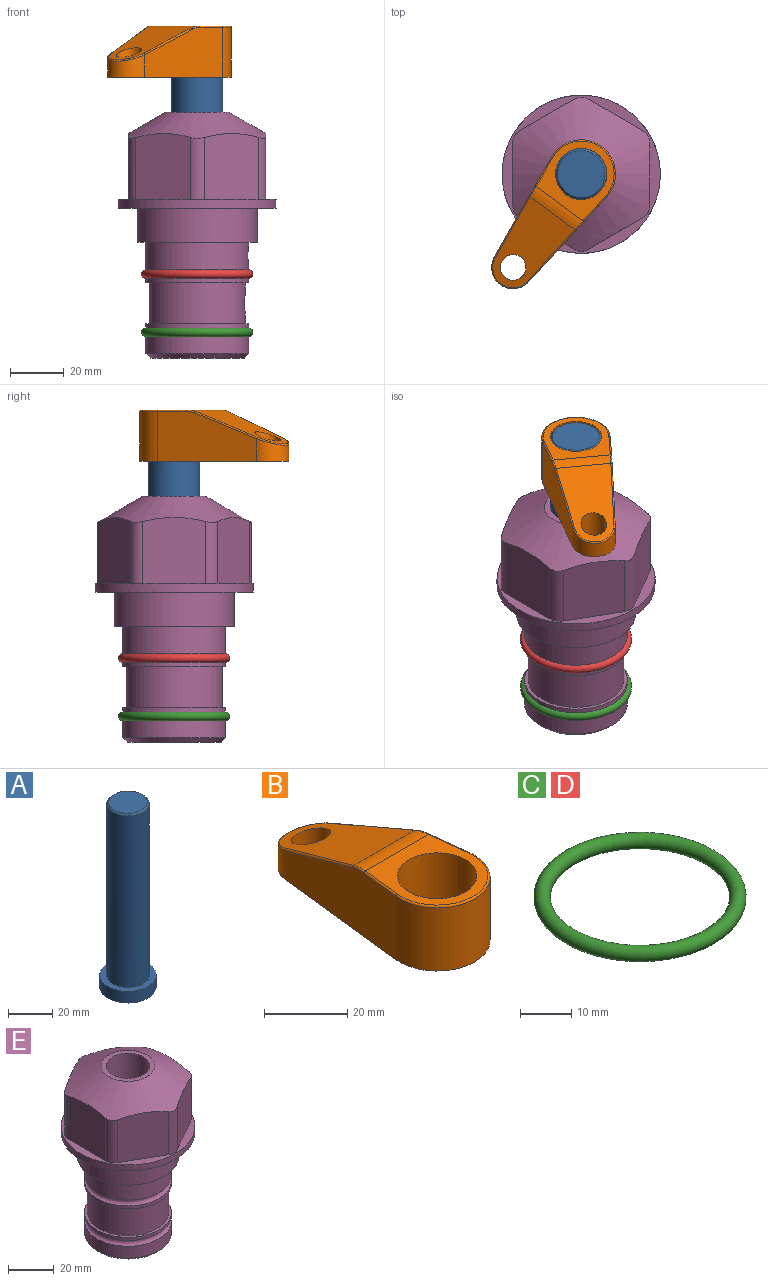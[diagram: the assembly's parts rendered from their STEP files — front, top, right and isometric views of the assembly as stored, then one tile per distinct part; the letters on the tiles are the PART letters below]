
ASSEMBLY  parts=5 mates=3
PART A: 6 faces, bbox 25.4x25.4x101.6 mm
  f0: plane 17.46x17.46mm, normal (0,0,1), area 239.5mm2, adj f5
  f1: plane 25.4x25.4mm, normal (0,0,-1), area 506.7mm2, adj f2
  f2: cylinder r=12.7mm len=25.4mm, axis (0,0,1), area 506.7mm2, adj f1,f3
  f3: plane 25.4x25.4mm, normal (0,0,1), area 221.7mm2, adj f2,f4
  f4: cylinder r=9.53mm len=94.46mm, axis (0,0,1), area 5653mm2, adj f3,f5
  f5: cone r=8.73mm half-angle=45deg, axis (0,0,-1), area 64.4mm2, adj f0,f4
PART B: 44 faces, bbox 27.5x64.5x19.1 mm
  f0: plane 2.3x0.95mm, normal (0,0,-1), area 1mm2, adj f25,f30,f34
  f1: plane 63.5x25.4mm, normal (0,0,-1), area 561.7mm2, adj f2,f3,f4,f5,f6,f7,f19,f20
  f2: cylinder r=12.7mm len=25.4mm, axis (0,0,-1), area 792.2mm2, adj f1,f3,f5,f13
  f3: plane 42.33x18.54mm, normal (0.99,0.11,0), area 647mm2, adj f1,f2,f4,f11,f12,f14
  f4: cylinder r=7.94mm len=15.78mm, axis (0,0,-1), area 158.6mm2, adj f1,f3,f5,f16
  f5: plane 42.33x18.54mm, normal (-0.99,0.11,0), area 647mm2, adj f1,f2,f4,f15,f17,f18
  f6: cylinder r=9.53mm len=19.05mm, axis (0,0,-1), area 1140.1mm2, adj f1,f8
  f7: cylinder r=4.76mm len=10.98mm, axis (0,0,-1), area 276.1mm2, adj f1,f9
  f8: plane 25.83x24.38mm, normal (0,0,1), area 262.2mm2, adj f6,f10,f11,f13,f15
  f9: plane 32.49x20.55mm, normal (0,0.34,0.94), area 489.9mm2, adj f7,f10,f14,f16,f18
  f10: cylinder r=12.7mm len=21.49mm, axis (-1,0,0), area 93.2mm2, adj f8,f9,f12,f17
  f11: cylinder r=0.51mm len=12.34mm, axis (0.11,-0.99,0), area 9.9mm2, adj f3,f8,f12,f13
  f12: bspline ~7.62x1.64mm, area 3.5mm2, adj f3,f10,f11,f14
  f13: torus R=12.19mm, axis (0,0,1), area 33.6mm2, adj f2,f8,f11,f15
  f14: cylinder r=0.51mm len=26.01mm, axis (0.1,-0.93,0.34), area 21.6mm2, adj f3,f9,f12,f16
  f15: cylinder r=0.51mm len=12.34mm, axis (0.11,0.99,0), area 9.9mm2, adj f5,f8,f13,f17
  f16: bspline ~15.78x7.05mm, area 15.7mm2, adj f4,f9,f14,f18
  f17: bspline ~7.62x1.64mm, area 3.5mm2, adj f5,f10,f15,f18
  f18: cylinder r=0.51mm len=26.01mm, axis (0.1,0.93,-0.34), area 21.6mm2, adj f5,f9,f16,f17
  f19: plane 21.6x14.29mm, normal (-0.99,-0.11,0), area 242.6mm2, adj f1,f26,f28,f34,f36,f38
  f20: plane 21.6x14.29mm, normal (0.99,-0.11,0), area 242.6mm2, adj f1,f27,f29,f37,f39,f41
  f21: cylinder r=12.7mm len=14.29mm, axis (0,0,-1), area 173.2mm2, adj f1,f26,f27,f30,f31,f33
  f22: cylinder r=7.94mm len=7.63mm, axis (0,0,-1), area 53.8mm2, adj f1,f28,f29,f42
  f23: plane 2.3x0.95mm, normal (0,0,-1), area 1mm2, adj f25,f33,f37
  f24: plane 17.94x12.32mm, normal (0,-0.34,-0.94), area 191.2mm2, adj f25,f38,f41,f42
  f25: cylinder r=9.53mm len=12.93mm, axis (-1,0,0), area 37.5mm2, adj f0,f23,f24,f31,f36,f39
  f26: cylinder r=1.59mm len=14.29mm, axis (0,0,-1), area 49mm2, adj f1,f19,f21,f32
  f27: cylinder r=1.59mm len=14.29mm, axis (0,0,-1), area 49mm2, adj f1,f20,f21,f35
  f28: cylinder r=1.59mm len=7.28mm, axis (0,0,-1), area 22.1mm2, adj f1,f19,f22,f40
  f29: cylinder r=1.59mm len=7.28mm, axis (0,0,-1), area 22.1mm2, adj f1,f20,f22,f43
  f30: torus R=14.29mm, axis (0,0,1), area 5.8mm2, adj f0,f21,f31,f32
  f31: bspline ~11.06x2.73mm, area 20.8mm2, adj f21,f25,f30,f33
  f32: sphere r=1.59mm, area 5.4mm2, adj f26,f30,f34
  f33: torus R=14.29mm, axis (0,0,1), area 5.8mm2, adj f21,f23,f31,f35
  f34: cylinder r=1.59mm len=1.68mm, axis (-0.11,0.99,0), area 2.4mm2, adj f0,f19,f32,f36
  f35: sphere r=1.59mm, area 5.4mm2, adj f27,f33,f37
  f36: bspline ~5.82x2.33mm, area 7.7mm2, adj f19,f25,f34,f38
  f37: cylinder r=1.59mm len=1.68mm, axis (0.11,0.99,0), area 2.4mm2, adj f20,f23,f35,f39
  f38: cylinder r=1.59mm len=18.33mm, axis (0.1,-0.93,0.34), area 46.7mm2, adj f19,f24,f36,f40
  f39: bspline ~5.82x2.33mm, area 7.7mm2, adj f20,f25,f37,f41
  f40: sphere r=1.59mm, area 3.6mm2, adj f28,f38,f42
  f41: cylinder r=1.59mm len=18.33mm, axis (0.1,0.93,-0.34), area 46.7mm2, adj f20,f24,f39,f43
  f42: bspline ~8.31x1.84mm, area 15.3mm2, adj f22,f24,f40,f43
  f43: sphere r=1.59mm, area 3.6mm2, adj f29,f41,f42
PART C: 1 faces, bbox 44.7x44.7x3.2 mm
  f0: torus R=19.05mm, axis (0,0,1), area 1193.9mm2
PART D: same geometry as C
PART E: 36 faces, bbox 58.7x58.7x91.2 mm
  f0: cylinder r=17.78mm len=35.56mm, axis (0,0,1), area 1670.8mm2, adj f23,f24,f31
  f1: cylinder r=19.05mm len=38.1mm, axis (0,0,1), area 1191.9mm2, adj f26,f27,f30
  f2: plane 58.66x58.66mm, normal (0,0,-1), area 1150.6mm2, adj f3,f28
  f3: cylinder r=29.33mm len=58.66mm, axis (0,0,-1), area 585.1mm2, adj f2,f4
  f4: plane 58.66x58.66mm, normal (0,0,1), area 475.9mm2, adj f3,f5,f6,f7,f8,f9,f10,f11
  f5: plane 24.5x20.32mm, normal (-0.5,0.87,0), area 562.8mm2, adj f4,f15,f16,f17
  f6: plane 24.5x20.32mm, normal (0.5,0.87,0), area 562.8mm2, adj f4,f14,f15,f17
  f7: plane 24.5x23.48mm, normal (1,0,0), area 562.8mm2, adj f4,f13,f14,f17
  f8: plane 24.5x20.32mm, normal (0.5,-0.87,0), area 562.8mm2, adj f4,f12,f13,f17
  f9: plane 24.5x20.32mm, normal (-0.5,-0.87,0), area 562.8mm2, adj f4,f11,f12,f17
  f10: plane 24.5x23.48mm, normal (-1,0,0), area 562.8mm2, adj f4,f11,f16,f17
  f11: cylinder r=5.08mm len=23.01mm, axis (0,0,-1), area 121.2mm2, adj f4,f9,f10,f17
  f12: cylinder r=5.08mm len=23.01mm, axis (0,0,-1), area 121.2mm2, adj f4,f8,f9,f17
  f13: cylinder r=5.08mm len=23.01mm, axis (0,0,-1), area 121.2mm2, adj f4,f7,f8,f17
  f14: cylinder r=5.08mm len=23.01mm, axis (0,0,-1), area 121.2mm2, adj f4,f6,f7,f17
  f15: cylinder r=5.08mm len=23.01mm, axis (0,0,-1), area 121.2mm2, adj f4,f5,f6,f17
  f16: cylinder r=5.08mm len=23.01mm, axis (0,0,-1), area 121.2mm2, adj f4,f5,f10,f17
  f17: cone r=11.73mm half-angle=60deg, axis (0,0,-1), area 2071.8mm2, adj f5,f6,f7,f8,f9,f10,f11,f12
  f18: plane 23.46x23.46mm, normal (0,0,1), area 147.4mm2, adj f17,f35
  f19: plane 34.93x34.93mm, normal (0,0,-1), area 958mm2, adj f29
  f20: cylinder r=19.05mm len=38.1mm, axis (0,0,1), area 760.1mm2, adj f21,f29
  f21: torus R=19.05mm, axis (0,0,1), area 565.3mm2, adj f20,f22
  f22: cylinder r=19.05mm len=38.1mm, axis (0,0,1), area 190mm2, adj f21,f23
  f23: plane 38.1x38.1mm, normal (0,0,1), area 146.9mm2, adj f0,f22
  f24: plane 38.1x38.1mm, normal (0,0,-1), area 146.9mm2, adj f0,f25
  f25: cylinder r=19.05mm len=38.1mm, axis (0,0,1), area 190mm2, adj f24,f26
  f26: torus R=19.05mm, axis (0,0,1), area 565.3mm2, adj f1,f25
  f27: plane 44.45x44.45mm, normal (0,0,-1), area 411.7mm2, adj f1,f28
  f28: cylinder r=22.23mm len=44.45mm, axis (0,0,1), area 1773.5mm2, adj f2,f27
  f29: cone r=19.05mm half-angle=45deg, axis (0,0,1), area 257.5mm2, adj f19,f20
  f30: cylinder r=3.17mm len=6.75mm, axis (-1,0,0), area 128mm2, adj f1,f33
  f31: cylinder r=3.17mm len=6.35mm, axis (-1,0,0), area 102.5mm2, adj f0,f33
  f32: plane 25.4x25.4mm, normal (0,0,1), area 506.7mm2, adj f33
  f33: cylinder r=12.7mm len=66.42mm, axis (0,0,-1), area 5236.2mm2, adj f30,f31,f32,f34
  f34: cone r=9.53mm half-angle=30deg, axis (0,0,-1), area 443.4mm2, adj f33,f35
  f35: cylinder r=9.53mm len=19.05mm, axis (0,0,-1), area 849mm2, adj f18,f34
PLACE A rot(axis=(0,0,-1),126.1deg) t=(0,0,-6.13)mm
PLACE B rot(axis=(0,0,1),143.9deg) t=(0,0,48.48)mm
PLACE C t=(0,0,-21.59)mm
PLACE D at identity
PLACE E at identity fixed
MATE fastened C.f0 <-> E.f0  axis (0,0,1) through (0,0,-46.1)mm
MATE cylindrical A.f2 <-> E.f0  axis (0,0,1) through (0,0,19.51)mm
MATE fastened B.f2 <-> A.f2  axis (0,0,1) through (0,0,67.53)mm
